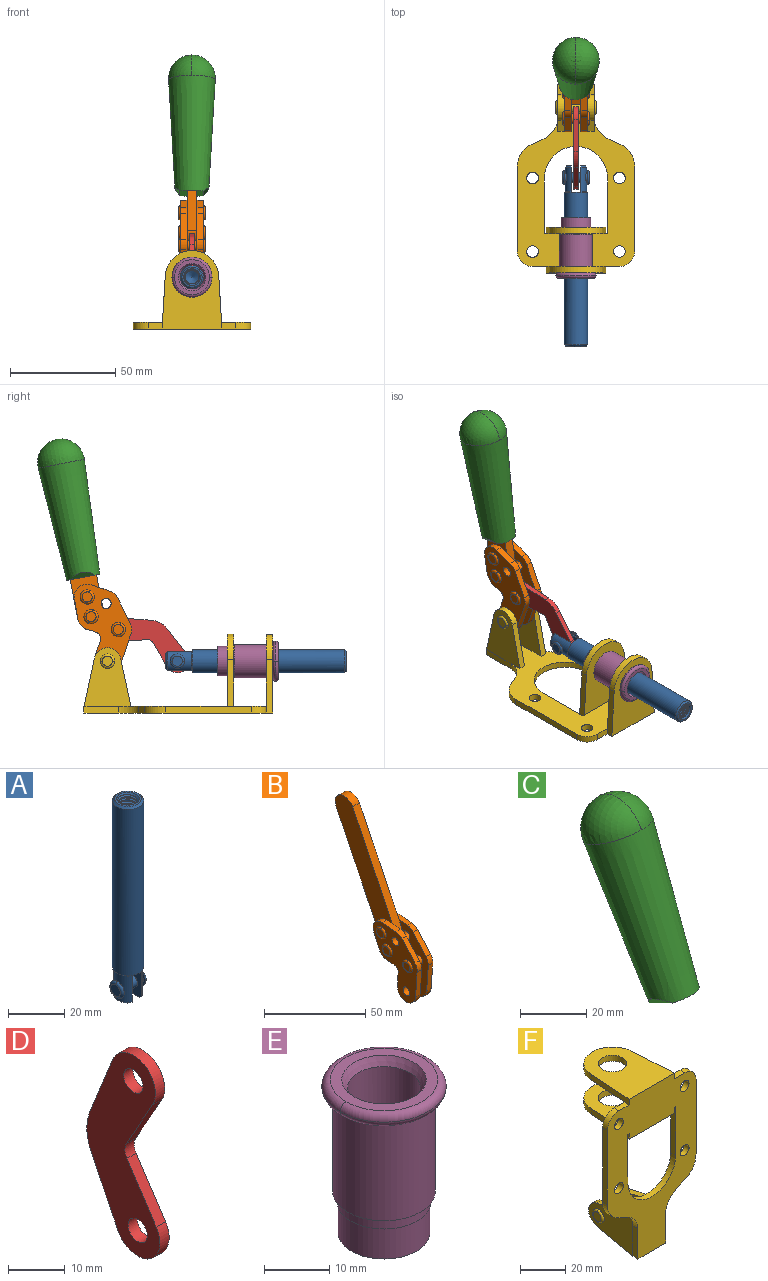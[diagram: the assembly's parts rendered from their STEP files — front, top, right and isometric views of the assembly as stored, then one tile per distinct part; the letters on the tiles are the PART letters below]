
ASSEMBLY  parts=6 mates=6
PART A: 48 faces, bbox 12.6x11.1x86.1 mm
  f0: torus R=2.41mm, axis (-1,0,0), area 15mm2, adj f30,f32,f34
  f1: torus R=2.41mm, axis (-1,0,0), area 15mm2, adj f29,f31,f33
  f2: cylinder r=5.54mm len=72.39mm, axis (0,0,1), area 2518.5mm2, adj f3,f4,f42,f43
  f3: cone r=5.54mm half-angle=45deg, axis (0,0,1), area 7.6mm2, adj f2,f5,f41
  f4: cone r=5.54mm half-angle=45deg, axis (0,0,-1), area 34.9mm2, adj f2,f39
  f5: cylinder r=5.08mm len=11.48mm, axis (0,0,1), area 108.3mm2, adj f3,f7,f8,f41
  f6: cylinder r=2.41mm len=4.83mm, axis (-1,0,0), area 71.2mm2, adj f40,f41
  f7: cylinder r=2.41mm len=4.83mm, axis (-1,0,0), area 7.6mm2, adj f5,f34
  f8: cone r=5.08mm half-angle=45deg, axis (0,0,1), area 10.6mm2, adj f5,f37,f41
  f9: cone r=3.98mm half-angle=45deg, axis (0,0,1), area 17.6mm2, adj f27,f39,f45,f46,f47
  f10: cylinder r=2.41mm len=4.83mm, axis (-1,0,0), area 7.6mm2, adj f33,f38
  f11: cylinder r=3.2mm len=6.4mm, axis (0,0,1), area 78.4mm2, adj f12,f28,f44,f45,f47
  f12: cylinder r=3.2mm len=6.4mm, axis (0,0,1), area 10.5mm2, adj f11,f13,f45,f47
  f13: cylinder r=3.2mm len=6.4mm, axis (0,0,1), area 10.5mm2, adj f12,f14,f45,f47
  f14: cylinder r=3.2mm len=6.4mm, axis (0,0,1), area 10.5mm2, adj f13,f15,f45,f47
  f15: cylinder r=3.2mm len=6.4mm, axis (0,0,1), area 10.5mm2, adj f14,f16,f45,f47
  f16: cylinder r=3.2mm len=6.4mm, axis (0,0,1), area 10.5mm2, adj f15,f17,f45,f47
  f17: cylinder r=3.2mm len=6.4mm, axis (0,0,1), area 10.5mm2, adj f16,f18,f45,f47
  f18: cylinder r=3.2mm len=6.4mm, axis (0,0,1), area 10.5mm2, adj f17,f19,f45,f47
  f19: cylinder r=3.2mm len=6.4mm, axis (0,0,1), area 10.5mm2, adj f18,f20,f45,f47
  f20: cylinder r=3.2mm len=6.4mm, axis (0,0,1), area 10.5mm2, adj f19,f21,f45,f47
  f21: cylinder r=3.2mm len=6.4mm, axis (0,0,1), area 10.5mm2, adj f20,f22,f45,f47
  f22: cylinder r=3.2mm len=6.4mm, axis (0,0,1), area 10.5mm2, adj f21,f23,f45,f47
  f23: cylinder r=3.2mm len=6.4mm, axis (0,0,1), area 10.5mm2, adj f22,f24,f45,f47
  f24: cylinder r=3.2mm len=6.4mm, axis (0,0,1), area 10.5mm2, adj f23,f25,f45,f47
  f25: cylinder r=3.2mm len=6.4mm, axis (0,0,1), area 10.5mm2, adj f24,f26,f45,f47
  f26: cylinder r=3.2mm len=6.4mm, axis (0,0,1), area 10.5mm2, adj f25,f27,f45,f47
  f27: cylinder r=3.2mm len=6.4mm, axis (0,0,1), area 7.4mm2, adj f9,f26,f45,f47
  f28: cone r=3.2mm half-angle=60deg, axis (0,0,1), area 37.2mm2, adj f11
  f29: plane 4.83x4.83mm, normal (-1,0,0), area 18.3mm2, adj f1,f31
  f30: plane 4.83x4.83mm, normal (1,0,0), area 18.3mm2, adj f0,f32
  f31: torus R=2.41mm, axis (-1,0,0), area 15mm2, adj f1,f29,f33
  f32: torus R=2.41mm, axis (-1,0,0), area 15mm2, adj f0,f30,f34
  f33: plane 6.83x6.83mm, normal (1,0,0), area 18.3mm2, adj f1,f10,f31
  f34: plane 6.83x6.83mm, normal (-1,0,0), area 18.3mm2, adj f0,f7,f32
  f35: cone r=5.08mm half-angle=45deg, axis (0,0,1), area 10.6mm2, adj f36,f38,f40
  f36: plane 7.25x1.97mm, normal (0,0,-1), area 10mm2, adj f35,f40
  f37: plane 7.25x1.97mm, normal (0,0,-1), area 10mm2, adj f8,f41
  f38: cylinder r=5.08mm len=11.48mm, axis (0,0,1), area 108.3mm2, adj f10,f35,f40,f42
  f39: plane 9.55x9.55mm, normal (0,0,1), area 22mm2, adj f4,f9
  f40: plane 12.76x10.09mm, normal (1,0,0), area 95.7mm2, adj f6,f35,f36,f38,f42,f43
  f41: plane 12.76x10.09mm, normal (-1,0,0), area 95.7mm2, adj f3,f5,f6,f8,f37,f43
  f42: cone r=5.54mm half-angle=45deg, axis (0,0,1), area 7.6mm2, adj f2,f38,f40
  f43: plane 11.07x4.7mm, normal (0,0,-1), area 50.4mm2, adj f2,f40,f41
  f44: plane 0.89x0.62mm, normal (-1,0,0), area 0.3mm2, adj f11,f45,f46,f47
  f45: bspline ~24.8x7.63mm, area 266.6mm2, adj f9,f11,f12,f13,f14,f15,f16,f17
  f46: bspline ~24.87x7.63mm, area 73.6mm2, adj f9,f44,f45,f47
  f47: bspline ~24.98x7.63mm, area 272.5mm2, adj f9,f11,f12,f13,f14,f15,f16,f17
PART B: 59 faces, bbox 12.9x60.2x99.6 mm
  f0: torus R=2.39mm, axis (-1,0,0), area 14.9mm2, adj f20,f43,f51
  f1: torus R=2.39mm, axis (-1,0,0), area 14.9mm2, adj f19,f42,f51
  f2: torus R=2.39mm, axis (-1,0,0), area 14.9mm2, adj f18,f35,f51
  f3: torus R=2.39mm, axis (-1,0,0), area 14.9mm2, adj f14,f17,f23
  f4: torus R=2.39mm, axis (-1,0,0), area 14.9mm2, adj f13,f16,f23
  f5: torus R=2.39mm, axis (-1,0,0), area 14.9mm2, adj f12,f15,f23
  f6: cylinder r=2.39mm len=4.78mm, axis (1,0,0), area 46.5mm2, adj f48,f50,f51
  f7: cylinder r=2.39mm len=4.78mm, axis (1,0,0), area 46.5mm2, adj f50,f51
  f8: cylinder r=6.35mm len=12.68mm, axis (1,0,0), area 61.8mm2, adj f38,f39,f50,f51
  f9: cylinder r=2.39mm len=4.78mm, axis (-1,0,0), area 70.5mm2, adj f46,f50
  f10: cylinder r=2.39mm len=4.78mm, axis (-1,0,0), area 46.5mm2, adj f23,f45,f46
  f11: cylinder r=2.39mm len=4.78mm, axis (-1,0,0), area 46.5mm2, adj f23,f46
  f12: plane 4.78x4.78mm, normal (1,0,0), area 17.9mm2, adj f5,f15
  f13: plane 4.78x4.78mm, normal (1,0,0), area 17.9mm2, adj f4,f16
  f14: plane 4.78x4.78mm, normal (1,0,0), area 17.9mm2, adj f3,f17
  f15: torus R=2.39mm, axis (-1,0,0), area 14.9mm2, adj f5,f12,f23
  f16: torus R=2.39mm, axis (-1,0,0), area 14.9mm2, adj f4,f13,f23
  f17: torus R=2.39mm, axis (-1,0,0), area 14.9mm2, adj f3,f14,f23
  f18: plane 4.78x4.78mm, normal (-1,0,0), area 17.9mm2, adj f2,f35
  f19: plane 4.78x4.78mm, normal (-1,0,0), area 17.9mm2, adj f1,f42
  f20: plane 4.78x4.78mm, normal (-1,0,0), area 17.9mm2, adj f0,f43
  f21: plane 2.26x0.2mm, normal (1,0,0), area 0.2mm2, adj f31,f44
  f22: plane 2.26x0.2mm, normal (-1,0,0), area 0.2mm2, adj f41,f44
  f23: plane 39.37x30.77mm, normal (1,0,0), area 565.5mm2, adj f3,f4,f5,f10,f11,f15,f16,f17
  f24: cylinder r=6.1mm len=4.15mm, axis (-1,0,0), area 14.7mm2, adj f23,f25,f32,f46
  f25: plane 10.25x9.01mm, normal (0,-0.75,0.66), area 42.3mm2, adj f23,f24,f26,f46
  f26: cylinder r=6.35mm len=4.64mm, axis (-1,0,0), area 15.6mm2, adj f23,f25,f27,f46
  f27: plane 15.84x3.1mm, normal (0,-1,-0.07), area 49.2mm2, adj f23,f26,f28,f46
  f28: cylinder r=6.35mm len=12.68mm, axis (-1,0,0), area 61.8mm2, adj f23,f27,f29,f46
  f29: plane 8.11x3.1mm, normal (0,1,0.07), area 25.2mm2, adj f23,f28,f30,f46
  f30: cylinder r=3.05mm len=3.25mm, axis (-1,0,0), area 14.8mm2, adj f23,f29,f31,f46
  f31: plane 5.99x3.1mm, normal (0,0.07,-1), area 18.6mm2, adj f21,f23,f30,f44,f46
  f32: plane 9.5x3.1mm, normal (0,-0.07,1), area 29.5mm2, adj f23,f24,f33,f46,f47
  f33: cylinder r=6.1mm len=8.63mm, axis (-1,0,0), area 39.1mm2, adj f23,f32,f34,f47
  f34: plane 8.65x3.96mm, normal (0,0.91,-0.42), area 29.5mm2, adj f23,f33,f44,f47
  f35: torus R=2.39mm, axis (-1,0,0), area 14.9mm2, adj f2,f18,f51
  f36: plane 10.25x9.01mm, normal (0,-0.75,0.66), area 42.3mm2, adj f37,f49,f50,f51
  f37: cylinder r=6.35mm len=4.64mm, axis (1,0,0), area 15.6mm2, adj f36,f38,f50,f51
  f38: plane 15.84x3.1mm, normal (0,-1,-0.07), area 49.2mm2, adj f8,f37,f50,f51
  f39: plane 8.11x3.1mm, normal (0,1,0.07), area 25.2mm2, adj f8,f40,f50,f51
  f40: cylinder r=3.05mm len=3.25mm, axis (1,0,0), area 14.8mm2, adj f39,f41,f50,f51
  f41: plane 5.99x3.1mm, normal (0,0.07,-1), area 18.6mm2, adj f22,f40,f44,f50,f51
  f42: torus R=2.39mm, axis (-1,0,0), area 14.9mm2, adj f1,f19,f51
  f43: torus R=2.39mm, axis (-1,0,0), area 14.9mm2, adj f0,f20,f51
  f44: cylinder r=6.35mm len=12.12mm, axis (-1,0,0), area 128.9mm2, adj f21,f22,f23,f31,f34,f41,f46,f47
  f45: plane 2.65x1.35mm, normal (1,0,0), area 1mm2, adj f10,f55
  f46: plane 39.08x20.42mm, normal (-1,0,0), area 412.5mm2, adj f9,f10,f11,f24,f25,f26,f27,f28
  f47: plane 77.62x39.82mm, normal (1,0,0), area 850mm2, adj f32,f33,f34,f44,f53,f54,f55
  f48: plane 2.65x1.35mm, normal (-1,0,0), area 1mm2, adj f6,f55
  f49: cylinder r=6.1mm len=4.15mm, axis (1,0,0), area 14.7mm2, adj f36,f50,f51,f56
  f50: plane 39.08x20.42mm, normal (1,0,0), area 412.5mm2, adj f6,f7,f8,f9,f36,f37,f38,f39
  f51: plane 39.37x30.77mm, normal (-1,0,0), area 565.5mm2, adj f0,f1,f2,f6,f7,f8,f35,f36
  f52: plane 8.65x3.96mm, normal (0,0.91,-0.42), area 29.5mm2, adj f44,f51,f57,f58
  f53: plane 68.49x33.4mm, normal (0,0.9,-0.44), area 358.1mm2, adj f44,f47,f54,f58
  f54: cylinder r=6.35mm len=12.06mm, axis (1,0,0), area 93.7mm2, adj f47,f53,f55,f58
  f55: plane 68.49x33.4mm, normal (0,-0.9,0.44), area 358.1mm2, adj f44,f45,f46,f47,f48,f50,f54,f58
  f56: plane 9.5x3.1mm, normal (0,-0.07,1), area 29.5mm2, adj f49,f50,f51,f57,f58
  f57: cylinder r=6.1mm len=8.63mm, axis (1,0,0), area 39.1mm2, adj f51,f52,f56,f58
  f58: plane 77.62x39.82mm, normal (-1,0,0), area 850mm2, adj f44,f52,f53,f54,f55,f56,f57
PART C: 11 faces, bbox 22.3x42.6x64.5 mm
  f0: sphere r=11.13mm, area 411.4mm2, adj f1,f8
  f1: cone r=11.11mm half-angle=3.3deg, axis (0,0.44,0.9), area 3251.8mm2, adj f0,f7,f8,f9,f10
  f2: cylinder r=6.16mm len=11.7mm, axis (1,0,0), area 89.5mm2, adj f3,f4,f5,f6
  f3: plane 60.23x36.75mm, normal (-1,0,0), area 763.6mm2, adj f2,f4,f6,f10
  f4: plane 51.37x25.05mm, normal (0,0.9,-0.44), area 264.2mm2, adj f2,f3,f5,f10
  f5: plane 60.23x36.75mm, normal (1,0,0), area 763.6mm2, adj f2,f4,f6,f10
  f6: plane 51.37x25.05mm, normal (0,-0.9,0.44), area 264.2mm2, adj f2,f3,f5,f10
  f7: plane 9.95x5.95mm, normal (0.71,-0.31,-0.64), area 25.8mm2, adj f1,f10
  f8: sphere r=11.13mm, area 411.4mm2, adj f0,f1
  f9: plane 9.95x5.95mm, normal (-0.71,-0.31,-0.64), area 25.8mm2, adj f1,f10
  f10: plane 14.27x11.38mm, normal (0,-0.44,-0.9), area 106.7mm2, adj f1,f3,f4,f5,f6,f7,f9
PART D: 12 faces, bbox 2.3x18.2x42.8 mm
  f0: cylinder r=2.4mm len=4.8mm, axis (1,0,0), area 34.9mm2, adj f4,f11
  f1: cylinder r=10.41mm len=8.47mm, axis (1,0,0), area 20.2mm2, adj f4,f9,f10,f11
  f2: cylinder r=3.05mm len=3.16mm, axis (1,0,0), area 7.7mm2, adj f4,f6,f7,f11
  f3: cylinder r=2.4mm len=4.8mm, axis (1,0,0), area 34.9mm2, adj f4,f11
  f4: plane 42.81x18.23mm, normal (-1,0,0), area 414.1mm2, adj f0,f1,f2,f3,f5,f6,f7,f8
  f5: cylinder r=5.54mm len=10.67mm, axis (1,0,0), area 41.8mm2, adj f4,f6,f10,f11
  f6: plane 11.66x6.53mm, normal (0,-0.87,-0.49), area 30.9mm2, adj f2,f4,f5,f11
  f7: plane 11.17x7.33mm, normal (0,-0.84,0.55), area 30.9mm2, adj f2,f4,f8,f11
  f8: cylinder r=5.54mm len=10.51mm, axis (1,0,0), area 41.8mm2, adj f4,f7,f9,f11
  f9: plane 13.67x6.67mm, normal (0,0.9,-0.44), area 35.1mm2, adj f1,f4,f8,f11
  f10: plane 14.1x5.7mm, normal (0,0.93,0.37), area 35.1mm2, adj f1,f4,f5,f11
  f11: plane 42.81x18.23mm, normal (1,0,0), area 414.1mm2, adj f0,f1,f2,f3,f5,f6,f7,f8
PART E: 15 faces, bbox 20.6x20.6x28.7 mm
  f0: torus R=8.26mm, axis (0,0,1), area 56.8mm2, adj f1,f10,f12
  f1: torus R=8.26mm, axis (0,0,1), area 56.8mm2, adj f0,f6,f13
  f2: cylinder r=5.59mm len=25.91mm, axis (0,0,1), area 909.6mm2, adj f3,f4
  f3: cone r=6.86mm half-angle=45deg, axis (0,0,-1), area 70.2mm2, adj f2,f14
  f4: cone r=6.47mm half-angle=30deg, axis (0,0,1), area 66.7mm2, adj f2,f13
  f5: cylinder r=7.04mm len=14.07mm, axis (0,0,1), area 252.6mm2, adj f11,f14
  f6: torus R=8.26mm, axis (0,0,1), area 56.8mm2, adj f1,f12,f13
  f7: cylinder r=7.16mm len=14.33mm, axis (0,0,1), area 91.5mm2, adj f9,f11
  f8: cylinder r=7.86mm len=18.42mm, axis (0,0,1), area 909.6mm2, adj f9,f10
  f9: plane 15.72x15.72mm, normal (0,0,-1), area 33mm2, adj f7,f8
  f10: plane 16.51x16.51mm, normal (0,0,-1), area 19.9mm2, adj f0,f8,f12
  f11: plane 14.33x14.33mm, normal (0,0,-1), area 5.7mm2, adj f5,f7
  f12: torus R=8.26mm, axis (0,0,1), area 56.8mm2, adj f0,f6,f10
  f13: plane 16.51x16.51mm, normal (0,0,1), area 82.7mm2, adj f1,f4,f6
  f14: plane 14.07x14.07mm, normal (0,0,-1), area 7.8mm2, adj f3,f5
PART F: 55 faces, bbox 55.7x37.4x89.8 mm
  f0: torus R=2.41mm, axis (-1,0,0), area 15mm2, adj f11,f15,f25
  f1: torus R=2.41mm, axis (-1,0,0), area 15mm2, adj f10,f12,f22
  f2: cylinder r=2.78mm len=5.56mm, axis (0,-1,0), area 54.2mm2, adj f30,f54
  f3: cylinder r=14.99mm len=29.97mm, axis (0,-1,0), area 145.9mm2, adj f30,f49,f53,f54
  f4: cylinder r=2.78mm len=5.56mm, axis (0,-1,0), area 54.2mm2, adj f30,f54
  f5: cylinder r=2.78mm len=5.56mm, axis (0,-1,0), area 54.2mm2, adj f30,f54
  f6: cylinder r=2.78mm len=5.56mm, axis (0,-1,0), area 54.2mm2, adj f30,f54
  f7: cylinder r=6.35mm len=12.7mm, axis (0,0,1), area 123.6mm2, adj f27,f51
  f8: cylinder r=6.35mm len=12.7mm, axis (0,0,-1), area 124.7mm2, adj f21,f35
  f9: cylinder r=2.41mm len=11.18mm, axis (-1,0,0), area 169.4mm2, adj f16,f19
  f10: plane 4.83x4.83mm, normal (1,0,0), area 18.3mm2, adj f1,f12
  f11: plane 4.83x4.83mm, normal (-1,0,0), area 18.3mm2, adj f0,f15
  f12: torus R=2.41mm, axis (-1,0,0), area 15mm2, adj f1,f10,f22
  f13: cylinder r=6.35mm len=12.41mm, axis (1,0,0), area 53.4mm2, adj f18,f19,f22,f23
  f14: cylinder r=6.35mm len=12.41mm, axis (-1,0,0), area 53.4mm2, adj f16,f17,f24,f25
  f15: torus R=2.41mm, axis (-1,0,0), area 15mm2, adj f0,f11,f25
  f16: plane 27.86x22.35mm, normal (1,0,0), area 425.4mm2, adj f9,f14,f17,f24,f30
  f17: plane 22.86x4.97mm, normal (0,0.21,0.98), area 72.5mm2, adj f14,f16,f25,f30
  f18: plane 22.86x4.97mm, normal (0,0.21,0.98), area 72.5mm2, adj f13,f19,f22,f30
  f19: plane 27.86x22.35mm, normal (-1,0,0), area 425.4mm2, adj f9,f13,f18,f23,f30
  f20: cylinder r=12.7mm len=25.35mm, axis (0,0,-1), area 119.8mm2, adj f21,f34,f35,f36
  f21: plane 34.21x28.07mm, normal (0,0,-1), area 702.4mm2, adj f8,f20,f30,f34,f36
  f22: plane 27.96x22.45mm, normal (1,0,0), area 407.2mm2, adj f1,f12,f13,f18,f23,f30,f42,f43
  f23: plane 22.86x4.97mm, normal (0,0.21,-0.98), area 72.5mm2, adj f13,f19,f22,f44
  f24: plane 22.86x4.97mm, normal (0,0.21,-0.98), area 72.5mm2, adj f14,f16,f25,f44
  f25: plane 27.86x22.35mm, normal (-1,0,0), area 407.1mm2, adj f0,f14,f15,f17,f24,f30,f45,f46
  f26: plane 3.1x0.95mm, normal (0,0,-1), area 2.7mm2, adj f30,f49,f50,f54
  f27: plane 34.21x28.07mm, normal (0,0,1), area 702.4mm2, adj f7,f28,f30,f50,f52
  f28: cylinder r=12.7mm len=25.35mm, axis (0,0,1), area 118.8mm2, adj f27,f50,f51,f52
  f29: plane 3.1x0.95mm, normal (0,0,-1), area 2.7mm2, adj f30,f52,f53,f54
  f30: plane 86.54x55.63mm, normal (0,1,0), area 2362.9mm2, adj f2,f3,f4,f5,f6,f16,f17,f18
  f31: plane 40.56x3.1mm, normal (-1,0,0), area 125.7mm2, adj f30,f32,f48,f54
  f32: cylinder r=7.11mm len=7.11mm, axis (0,-1,0), area 34.6mm2, adj f30,f31,f33,f54
  f33: plane 6.67x3.1mm, normal (0,0,1), area 20.4mm2, adj f30,f32,f34,f54
  f34: plane 25.39x3.13mm, normal (-1,0.06,0), area 79.5mm2, adj f20,f21,f33,f35,f54
  f35: plane 37.31x28.45mm, normal (0,0,1), area 789.9mm2, adj f8,f20,f34,f36,f54
  f36: plane 25.39x3.13mm, normal (1,0.06,0), area 79.5mm2, adj f20,f21,f35,f37,f54
  f37: plane 6.67x3.1mm, normal (0,0,1), area 20.4mm2, adj f30,f36,f38,f54
  f38: cylinder r=7.11mm len=7.11mm, axis (0,-1,0), area 34.6mm2, adj f30,f37,f39,f54
  f39: plane 40.56x3.1mm, normal (1,0,0), area 125.7mm2, adj f30,f38,f40,f54
  f40: cylinder r=11.18mm len=10.16mm, axis (0,-1,0), area 39.5mm2, adj f30,f39,f41,f54
  f41: plane 6.09x3.1mm, normal (0.42,0,-0.91), area 20.8mm2, adj f30,f40,f42,f54
  f42: cylinder r=11.18mm len=9.41mm, axis (0,-1,0), area 37.2mm2, adj f22,f30,f41,f43,f54
  f43: plane 16.5x3.1mm, normal (1,0,0), area 51.1mm2, adj f22,f42,f44,f54
  f44: plane 17.37x3.1mm, normal (0,0,-1), area 53.8mm2, adj f23,f24,f30,f43,f45,f54
  f45: plane 16.5x3.1mm, normal (-1,0,0), area 51.1mm2, adj f25,f44,f46,f54
  f46: cylinder r=11.18mm len=9.41mm, axis (0,-1,0), area 37.2mm2, adj f25,f30,f45,f47,f54
  f47: plane 6.09x3.1mm, normal (-0.42,0,-0.91), area 20.8mm2, adj f30,f46,f48,f54
  f48: cylinder r=11.18mm len=10.16mm, axis (0,-1,0), area 39.5mm2, adj f30,f31,f47,f54
  f49: plane 26.54x3.1mm, normal (-1,0,0), area 82.3mm2, adj f3,f26,f30,f54
  f50: plane 25.39x3.1mm, normal (1,0.06,0), area 78.8mm2, adj f26,f27,f28,f51,f54
  f51: plane 37.31x28.45mm, normal (0,0,-1), area 789.9mm2, adj f7,f28,f50,f52,f54
  f52: plane 25.39x3.1mm, normal (-1,0.06,0), area 78.8mm2, adj f27,f28,f29,f51,f54
  f53: plane 26.54x3.1mm, normal (1,0,0), area 82.3mm2, adj f3,f29,f30,f54
  f54: plane 89.66x55.63mm, normal (0,-1,0), area 2678.5mm2, adj f2,f3,f4,f5,f6,f26,f29,f31
PLACE A rot(axis=(1,0,0),90deg) t=(0,15.65,0)mm
PLACE B rot(axis=(1,0,0),15deg) t=(0,1.24,49.24)mm
PLACE C rot(axis=(1,0,0),15deg) t=(-0.04,1.24,49.24)mm
PLACE D rot(axis=(0,-0.53,-0.85),180deg) t=(0,25.15,10.71)mm
PLACE E rot(axis=(1,0,0),90deg) t=(0,1.23,0)mm
PLACE F rot(axis=(1,0,0),90deg) t=(0,1.23,0)mm fixed
MATE revolute D.f5 <-> B.f4  axis (-1,0,0) through (0,28.16,39.62)mm
MATE revolute D.f3 <-> A.f6  axis (-1,0,0) through (0,0.18,24.61)mm
MATE slider F.f7 <-> A.f2  axis (0,-1,0) through (0,-45.16,24.61)mm
MATE fastened C.f2 <-> B.f54  axis (1,0,0) through (-2.35,55.69,120.54)mm
MATE fastened F.f7 <-> E.f2  axis (0,-1,0) through (0,-45.16,24.61)mm
MATE revolute B.f7 <-> F.f0  axis (-1,0,0) through (0,33.32,24.61)mm
